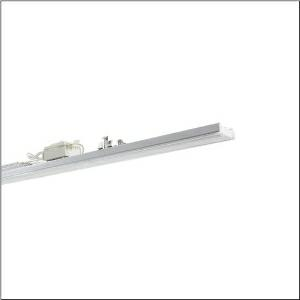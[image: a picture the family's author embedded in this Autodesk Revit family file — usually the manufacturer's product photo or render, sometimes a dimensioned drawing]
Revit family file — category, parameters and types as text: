
# Revit family: licross_11_recessed_mo_51te1ecn49xg
name_source: partatom
category: Lighting Fixtures
units: mm (PartAtom-declared; Revit-internal decimal feet)

## family parameters
Cut with Voids When Loaded = No
Host = Face
Light Source = No
Part Type = Normal
Room Calculation Point = No
Round Connector Dimension = Use Diameter
Shared = No

## types (1)
- --- (1 x LED, 9000 lm, 49.3 W, 4000K)
    Apparent Load = 49 VA
    CIE Flux Codes = 85 95 99 100 100
    Color Rendering = 80
    Color Temperature = 4000K
    Default Elevation = 1800 mm
    Description = Licross 11 Recessed MO, luminaire insert, of sheet steel, galvanised, coil coated, white, length: 1.500mm, width: 66mm, height: 67mm, LED rated luminous flux: 9.000lm, light colour: 840, SDCM (Standard Deviation of Colour Matching)MacAdam ≤ 2 SDCM (initial), control gear: ON/OFF Multilumen, CLOi, with plug, 3-pole, with phase selection, mains connection: 220..240V, AC, 50/60Hz, start of lifetime: 49W, end of service life: 55W, internal wiring halogen-free, primary light control with lens, of plastic, primary optical cover: cover, of PMMA, light emission: direct distribution, primary light characteristic: symmetric, protection rating (complete): IP54, insulation class (complete): insulation class I (protective earthing), certification: CE, ENEC, VDE, UKCA, protection symbol: D if used in an environment with non-conductive dust loads with corresponding accessories, impact resistance: IK06, permissible ambient temperature for indoor applications: -35..+40°C, corresponds to IFS (International Featured Standards) requirements for safety and quality in the food industry, reducing of maximum allowable ambient temperature of 5°C with ceiling mounting, LABS conformity tested according to VDMA 24364:2018-05, The light source and the operating device comply with the requirements of the Ecodesign Regulation (EU) 2019/2020 and are replaceable in accordance with this regulation, packaging unit: 1 piece
    Height = 58 mm
    Lamp = 1 x LED
    Lamp Light Flux = 9000 lm
    Lamp Power = 49.3 W
    Lamp count = 1
    Length = 1500 mm
    Luminous efficacy = 183 lm/W
    Manufacturer = Siteco
    ModVariant = No
    Model = 51TE1ECN49XG
    Mounting Place = Ceiling
    Mounting Type = Pendant
    Number of Poles = 1
    OnlyDefault = Yes
    Power Factor = 1
    Product Name = Licross 11 Recessed MO
    Product group = luminaire insert | ceiling pendant
    ProductGroupID = 901
    Protection Class = Protection class I
    Protection Degree = IP 54
    RLX_Detail_Level = 1
    RLX_Emergency_Light_Flux = 0 lm
    RLX_Emergency_Type = 0
    RLX_Emergency_Type_DB = No
    RlxData = <blob elided: 22685 chars, md5=c85a5587>
    Socket = socket
    Standby Power = 0 W
    System Light Flux = 9000 lm
    System Power = 49 W
    Type Comments = factory setting: luminous flux: 100 % | (A | C | E) | 113 mA
    Type Image = l_1296930.jpg
    URL = http://relux.com
    VarID = @adj_000081
    Voltage = 0 V
    Weight = 0.00 kg
    Width = 66 mm

## geometry (parser evidence)
native form markers: Blend x4, Sweep x11
no freeform markers — native parametric forms only
